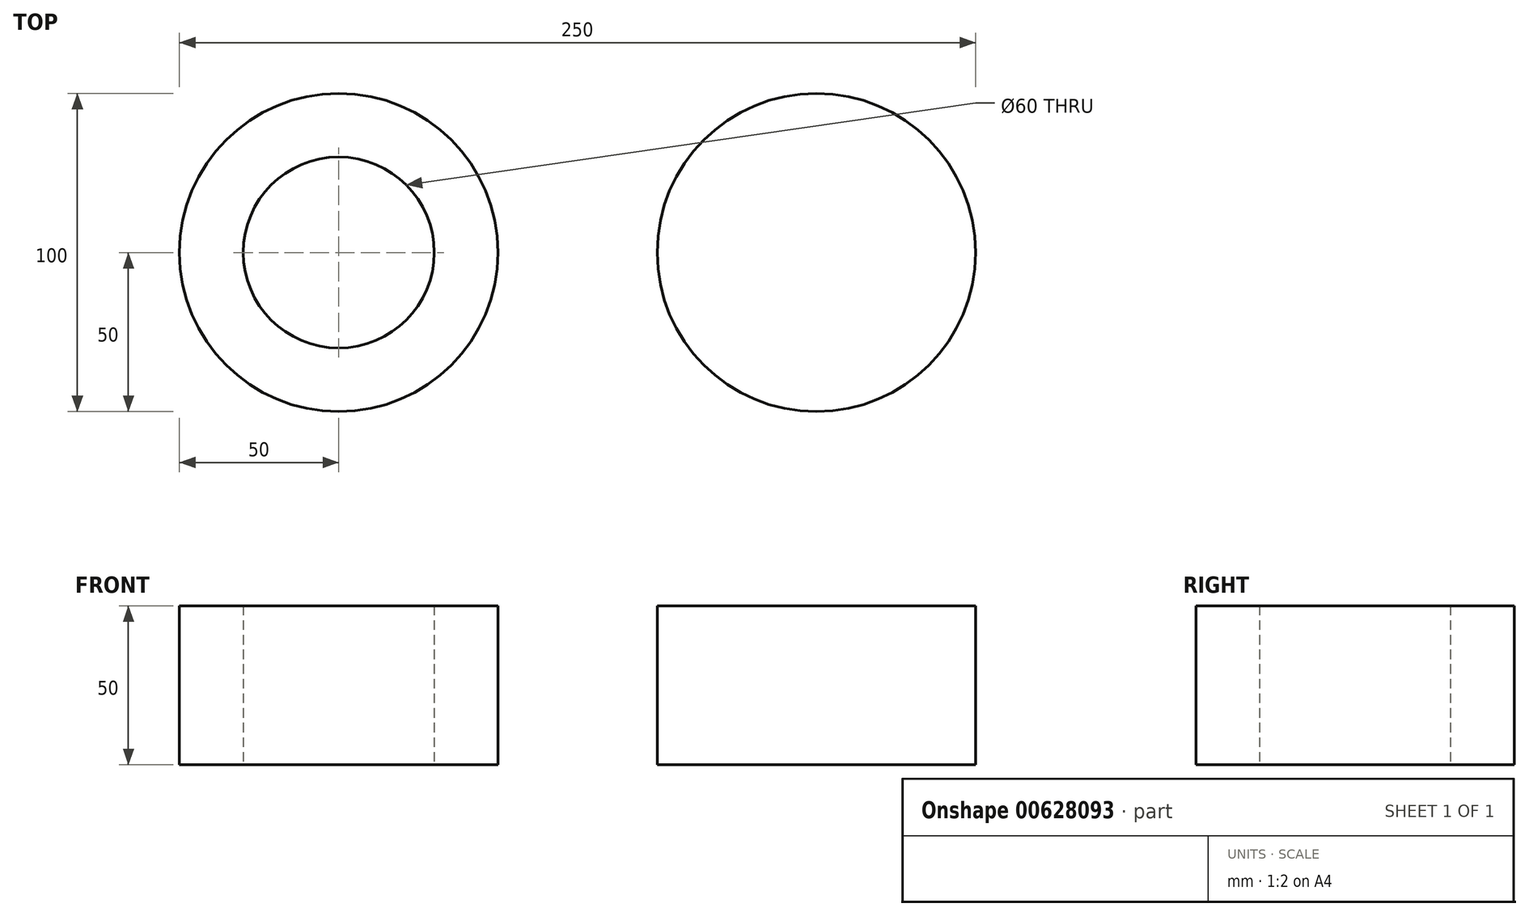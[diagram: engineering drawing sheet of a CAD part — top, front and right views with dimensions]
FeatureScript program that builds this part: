
annotation { "Feature Type Name" : "Feature", "Feature Type Description" : "" }
export const myFeature = defineFeature(function(context is Context, id is Id, definition is map)
    precondition{}
    {
        {
            var Q0;
            Q0=qCreatedBy(makeId("Top.planeOp"),FACE);
            var sketch = newSketch(context, id + "F0", { "sketchPlane" : qUnion([Q0])});
            skCircle(sketch, "E0", {"center": v(0, 0) * mm, "radius": 30 * mm});
            skCircle(sketch, "E1", {"center": v(0, 0) * mm, "radius": 50 * mm});
            skLineSegment(sketch, "E2", {"start": v(30, 0) * mm, "end": v(50, 0) * mm, "construction": true});
            skSolve(sketch);
        }
        {
            var Q0;
            Q0=makeQuery(id+"F0.imprint","IMPRINT",FACE,{"disambiguationData":[TD([[makeQuery(id+"F0.imprint","IMPRINT",EDGE,{"derivedFrom":sQuery(id+"F0.wireOp",EDGE,"E0")}),-1.0]])]});
            extrude(context, id + "F1", {"entities" : qUnion([Q0]), "depth" : 50 * mm, "offsetDistance" : 25 * mm});
        }
        {
            var Q0;
            Q0=makeQuery(id+"F0.imprint","IMPRINT",FACE,{"disambiguationData":[TD([[makeQuery(id+"F0.imprint","IMPRINT",EDGE,{"derivedFrom":sQuery(id+"F0.wireOp",EDGE,"E0")}),1.0]])]});
            var Q1;
            Q1=makeQuery(id+"F0.imprint","IMPRINT",FACE,{"disambiguationData":[TD([[makeQuery(id+"F0.imprint","IMPRINT",EDGE,{"derivedFrom":sQuery(id+"F0.wireOp",EDGE,"E0")}),-1.0]])]});
            extrude(context, id + "F2", {"entities" : qUnion([Q0, Q1]), "depth" : 50 * mm, "offsetDistance" : 25 * mm});
        }
        {
            var Q0;
            Q0=makeQuery(id+"F2.opExtrude","SWEPT_BODY",BODY,{"disambiguationData":[OSD([sQuery(id+"F0.wireOp",EDGE,"E1")])]});
            transform(context, id + "F3", {"entities" : qUnion([Q0]), "transformType" : TransformType.TRANSLATION_3D, "dx" : 150 * mm, "dy" : 0 * mm, "dz" : 0 * mm, "makeCopy" : false});
        }
    });
